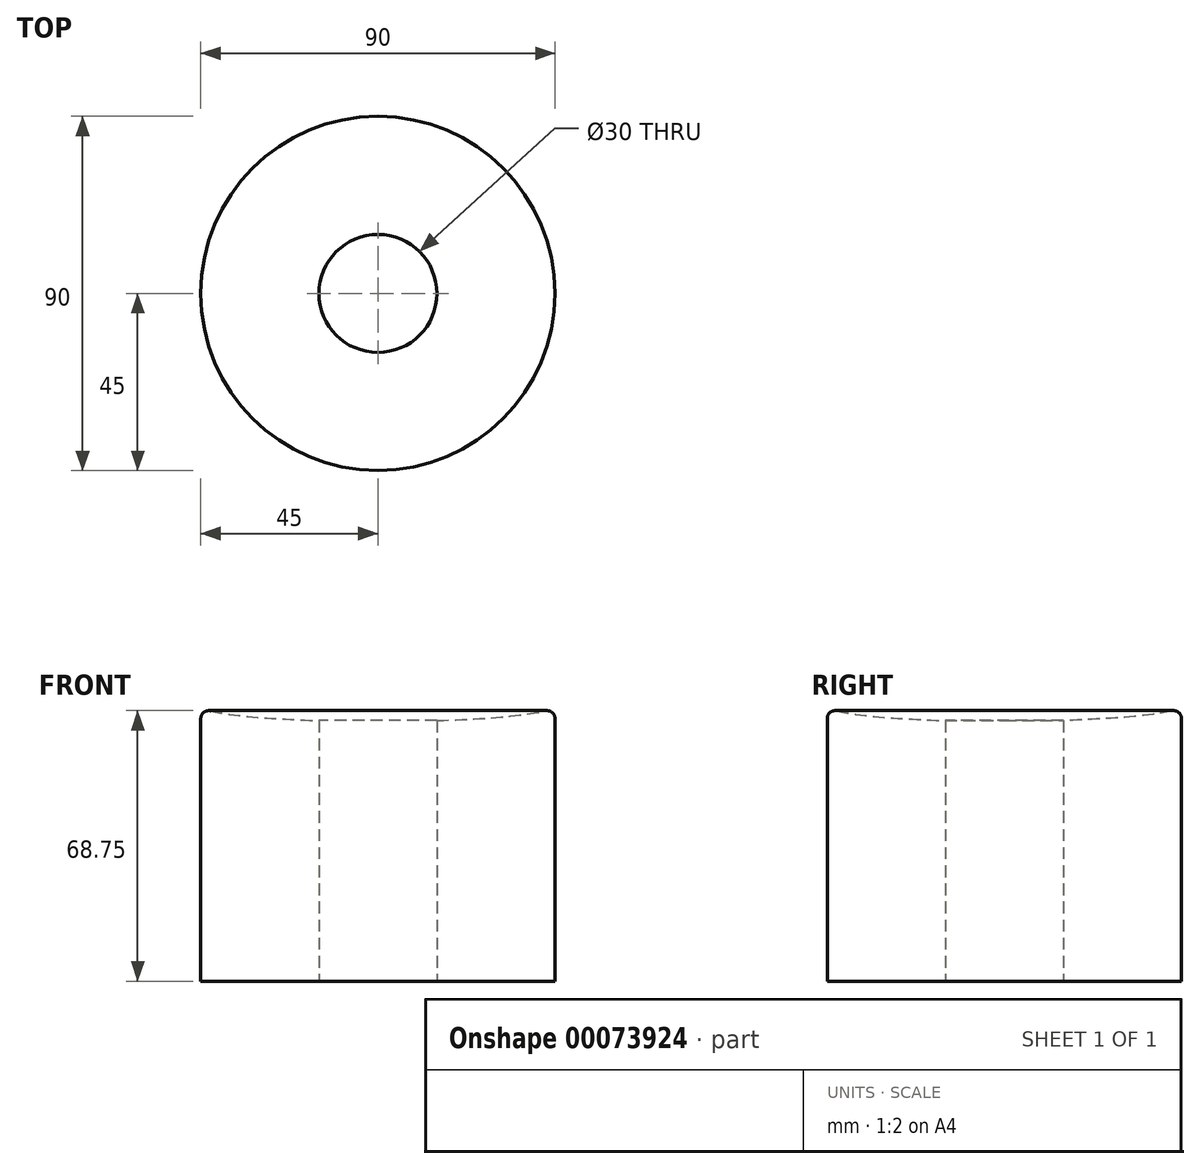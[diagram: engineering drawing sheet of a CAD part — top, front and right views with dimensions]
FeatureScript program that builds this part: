
annotation { "Feature Type Name" : "Feature", "Feature Type Description" : "" }
export const myFeature = defineFeature(function(context is Context, id is Id, definition is map)
    precondition{}
    {
        {
            var Q0;
            Q0=qCreatedBy(makeId("Top.planeOp"),FACE);
            var sketch = newSketch(context, id + "F0", { "sketchPlane" : qUnion([Q0])});
            skCircle(sketch, "E0", {"center": v(0, 0) * mm, "radius": 45 * mm});
            skSolve(sketch);
        }
        {
            var Q0;
            Q0=makeQuery(id+"F0.imprint","IMPRINT",FACE,{"disambiguationData":[TD([[makeQuery(id+"F0.imprint","IMPRINT",EDGE,{"derivedFrom":sQuery(id+"F0.wireOp",EDGE,"E0")}),1.0]])]});
            extrude(context, id + "F1", {"entities" : qUnion([Q0]), "depth" : 70 * mm});
        }
        {
            var Q0;
            Q0=qCreatedBy(makeId("Front.planeOp"),FACE);
            var sketch = newSketch(context, id + "F2", { "sketchPlane" : qUnion([Q0])});
            skLineSegment(sketch, "E1", {"start": v(0, 0) * mm, "end": v(0, 70) * mm});
            skLineSegment(sketch, "E2", {"start": v(0, 70) * mm, "end": v(0, 74) * mm});
            skLineSegment(sketch, "E3", {"start": v(0, 70) * mm, "end": v(45, 70) * mm});
            skEllipticalArc(sketch, "E4", {});
            const initialGuessF2  = {"E4": [0, 0.07, 1, 0, 0.045, 0.004, 4.71238898038469, 1.5707963267948966]};
            skSetInitialGuess(sketch, initialGuessF2);
            skSolve(sketch);
        }
        {
            var Q0;
            {var subQ0=sQuery(id+"F2.wireOp",EDGE,"E3");Q0=makeQuery(id+"F2.imprint","IMPRINT",FACE,{"disambiguationData":[TD([[makeQuery(id+"F2.imprint","IMPRINT",EDGE,{"derivedFrom":subQ0}),-1.0]])]});}
            var Q1;
            Q1=sQuery(id+"F2.wireOp",EDGE,"E1");
            revolve(context, id + "F3", {"operationType" : NewBodyOperationType.REMOVE, "entities" : qUnion([Q0]), "axis" : qUnion([Q1]), "revolveType" : RevolveType.FULL, "oppositeDirection" : true});
        }
        {
            var Q0;
            Q0=makeQuery(id+"F3.boolean.opBoolean","MERGE",EDGE,{"derivedFrom":[makeQuery(id+"F1.opExtrude","CAP_EDGE",EDGE,{"disambiguationData":[OSD([sQuery(id+"F0.wireOp",EDGE,"E0")])],"isStart":false}),makeQuery(id+"F3.opRevolve","SWEPT_EDGE",EDGE,{"disambiguationData":[OSD([sQuery(id+"F2.wireOp",EDGE,"E3"),sQuery(id+"F2.wireOp",EDGE,"E4")])]})]});
            fillet(context, id + "F4", {"entities" : qUnion([Q0]), "radius" : 2 * mm, "tangentPropagation" : true, "allowEdgeOverflow" : false});
        }
        {
            var Q0;
            Q0=qCreatedBy(makeId("Top.planeOp"),FACE);
            var sketch = newSketch(context, id + "F5", { "sketchPlane" : qUnion([Q0])});
            skCircle(sketch, "E5", {"center": v(0, 0) * mm, "radius": 15 * mm});
            skSolve(sketch);
        }
        {
            var Q0;
            Q0 = qSketchRegion(id + "F5", true);
            extrude(context, id + "F6", {"entities" : qUnion([Q0]), "operationType" : NewBodyOperationType.REMOVE, "depth" : 88.5 * mm});
        }
    });
